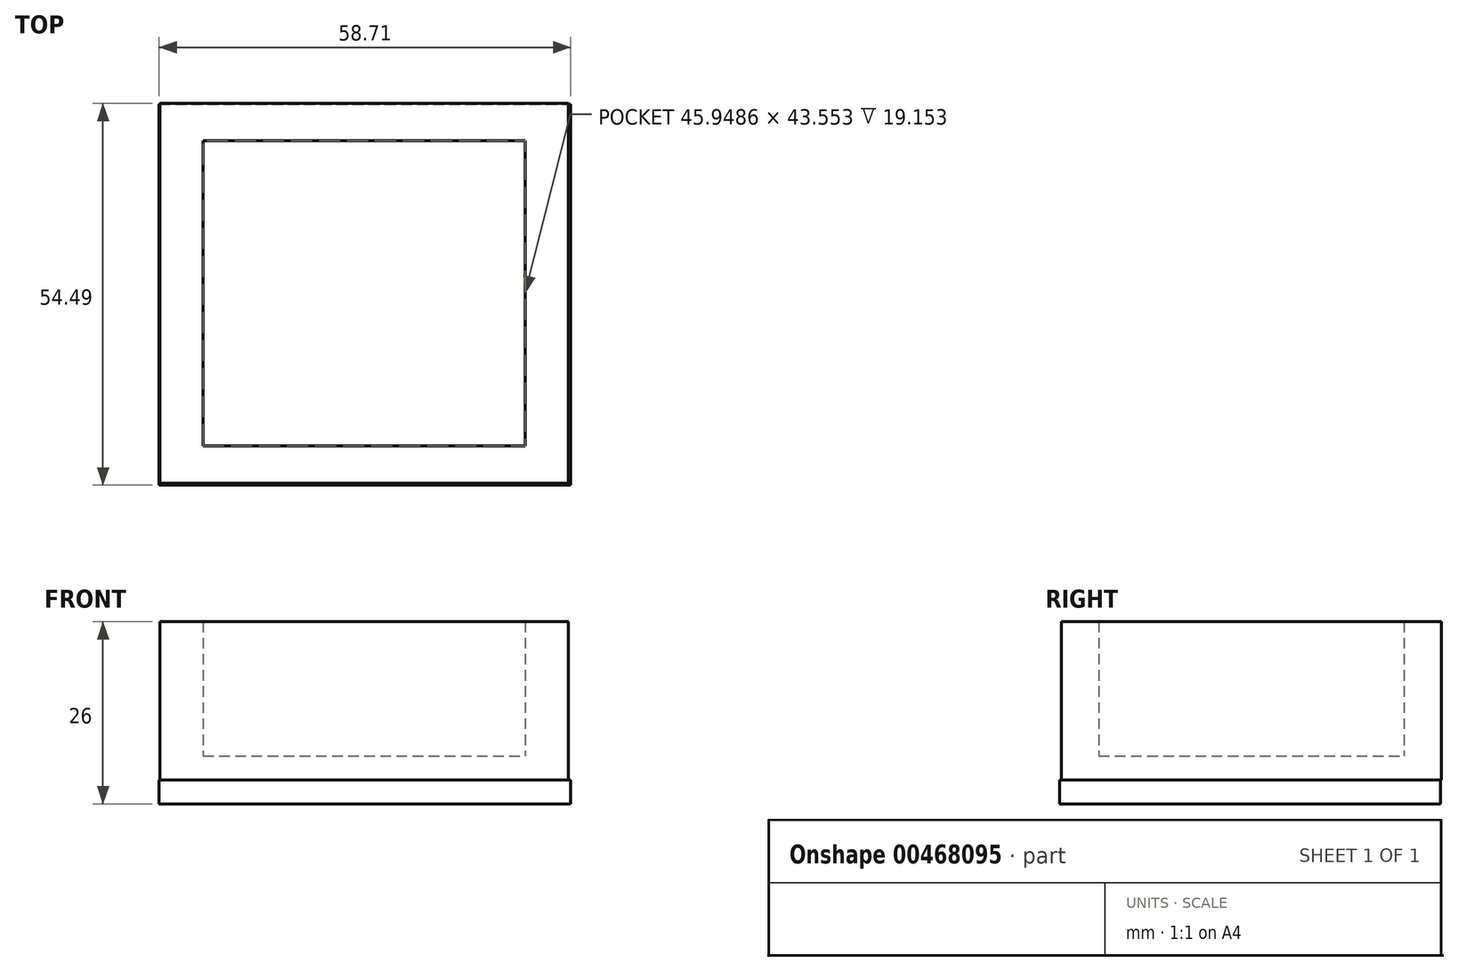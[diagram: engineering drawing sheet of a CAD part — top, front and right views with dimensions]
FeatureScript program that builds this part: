
annotation { "Feature Type Name" : "Feature", "Feature Type Description" : "" }
export const myFeature = defineFeature(function(context is Context, id is Id, definition is map)
    precondition{}
    {
        {
            var Q0;
            Q0=qCreatedBy(makeId("Top.planeOp"),FACE);
            var sketch = newSketch(context, id + "F0", { "sketchPlane" : qUnion([Q0])});
            skLineSegment(sketch, "E0.bottom", {"start": v(-29.15, -27.1) * mm, "end": v(29.15, -27.1) * mm});
            skLineSegment(sketch, "E0.top", {"start": v(-29.15, 27.1) * mm, "end": v(29.15, 27.1) * mm});
            skLineSegment(sketch, "E0.left", {"start": v(-29.15, -27.1) * mm, "end": v(-29.15, 27.1) * mm});
            skLineSegment(sketch, "E0.right", {"start": v(29.15, -27.1) * mm, "end": v(29.15, 27.1) * mm});
            skPoint(sketch, "E0.middle", {"position": v(0, 0) * mm});
            skLineSegment(sketch, "E1.bottom", {"start": v(-22.97, -21.78) * mm, "end": v(22.97, -21.78) * mm});
            skLineSegment(sketch, "E1.top", {"start": v(-22.97, 21.78) * mm, "end": v(22.97, 21.78) * mm});
            skLineSegment(sketch, "E1.left", {"start": v(-22.97, -21.78) * mm, "end": v(-22.97, 21.78) * mm});
            skLineSegment(sketch, "E1.right", {"start": v(22.97, -21.78) * mm, "end": v(22.97, 21.78) * mm});
            skSolve(sketch);
        }
        {
            var Q0;
            Q0=makeQuery(id+"F0.imprint","IMPRINT",FACE,{"disambiguationData":[TD([[makeQuery(id+"F0.imprint","IMPRINT",EDGE,{"derivedFrom":sQuery(id+"F0.wireOp",EDGE,"E0.bottom")}),1.0]])]});
            extrude(context, id + "F1", {"entities" : qUnion([Q0]), "depth" : 22.56 * mm});
        }
        {
            var Q0;
            Q0=makeQuery(id+"F0.imprint","IMPRINT",FACE,{"disambiguationData":[TD([[makeQuery(id+"F0.imprint","IMPRINT",EDGE,{"derivedFrom":sQuery(id+"F0.wireOp",EDGE,"E1.bottom")}),1.0]])]});
            extrude(context, id + "F2", {"entities" : qUnion([Q0]), "operationType" : NewBodyOperationType.ADD, "depth" : 3.4 * mm});
        }
        {
            var Q0;
            Q0=qCreatedBy(makeId("Top.planeOp"),FACE);
            var sketch = newSketch(context, id + "F3", { "sketchPlane" : qUnion([Q0])});
            skLineSegment(sketch, "E2.bottom", {"start": v(-29.25, 26.97) * mm, "end": v(29.46, 26.97) * mm});
            skLineSegment(sketch, "E2.top", {"start": v(-29.25, -27.38) * mm, "end": v(29.46, -27.38) * mm});
            skLineSegment(sketch, "E2.left", {"start": v(-29.25, 26.97) * mm, "end": v(-29.25, -27.38) * mm});
            skLineSegment(sketch, "E2.right", {"start": v(29.46, 26.97) * mm, "end": v(29.46, -27.38) * mm});
            skSolve(sketch);
        }
        {
            var Q0;
            Q0 = qSketchRegion(id + "F3", true);
            extrude(context, id + "F4", {"entities" : qUnion([Q0]), "oppositeDirection" : true, "depth" : 3.44 * mm});
        }
    });
